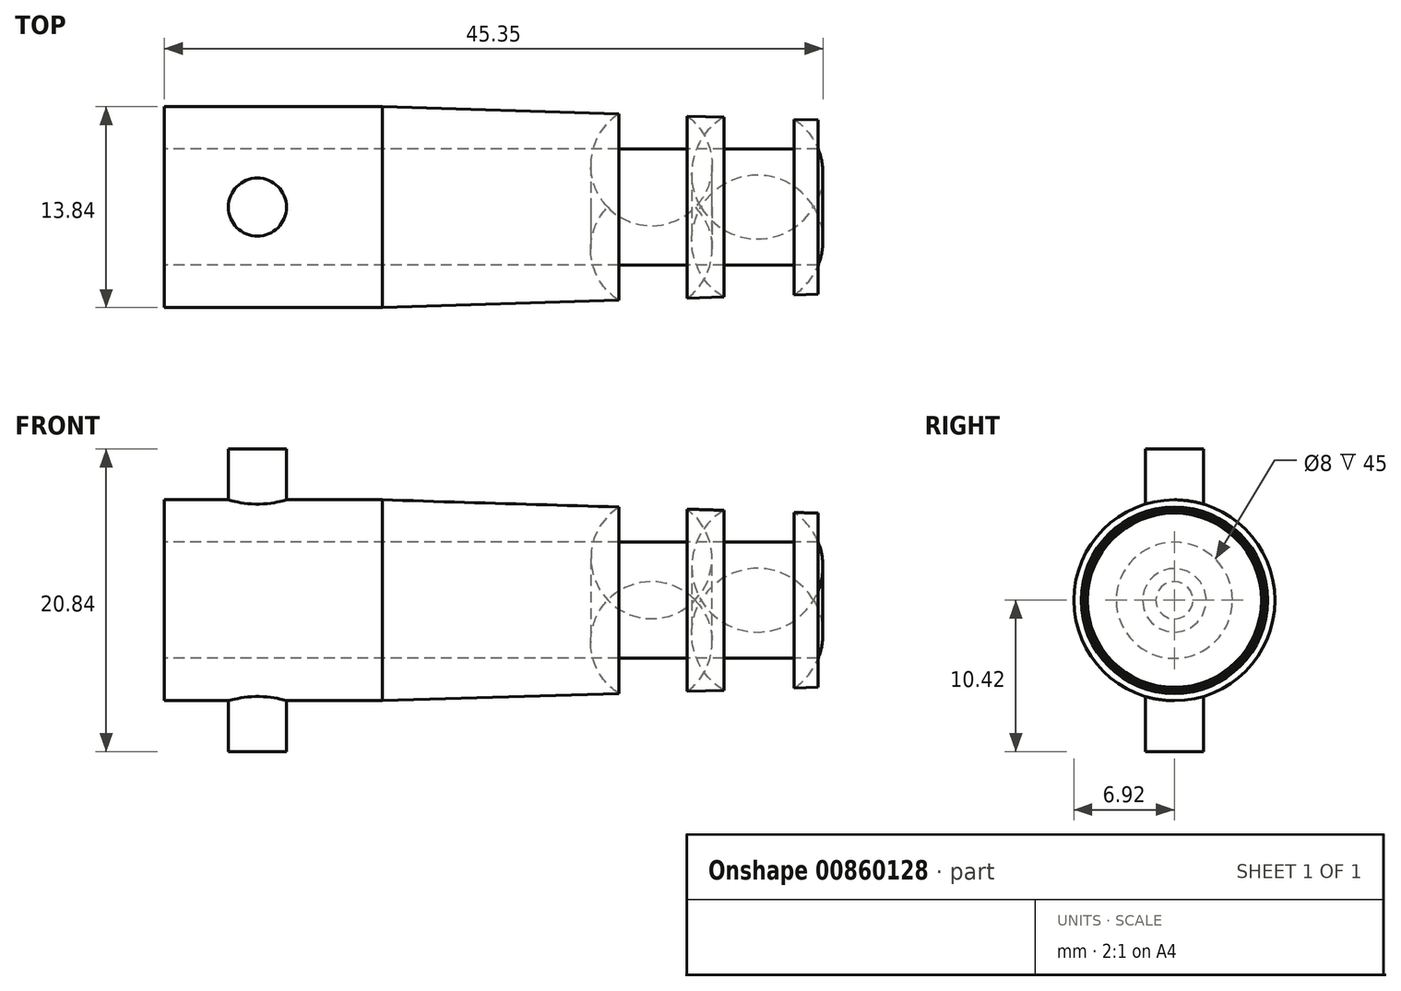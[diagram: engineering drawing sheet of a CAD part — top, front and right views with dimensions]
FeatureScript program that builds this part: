
annotation { "Feature Type Name" : "Feature", "Feature Type Description" : "" }
export const myFeature = defineFeature(function(context is Context, id is Id, definition is map)
    precondition{}
    {
        {
            var Q0;
            Q0=qCreatedBy(makeId("Front.planeOp"),FACE);
            var sketch = newSketch(context, id + "F0", { "sketchPlane" : qUnion([Q0])});
            skLineSegment(sketch, "E0", {"start": v(-34.69, 0) * mm, "end": v(10.31, 0) * mm});
            skLineSegment(sketch, "E1", {"start": v(10.31, 0) * mm, "end": v(10.31, 6) * mm});
            skLineSegment(sketch, "E2", {"start": v(-34.69, 6.92) * mm, "end": v(-19.69, 6.92) * mm});
            skLineSegment(sketch, "E3", {"start": v(-19.69, 6.92) * mm, "end": v(10.31, 6) * mm});
            skLineSegment(sketch, "E4", {"start": v(-34.69, 0) * mm, "end": v(-34.69, 6.92) * mm});
            skArc(sketch, "E5", {"start": v(8.68, 6.05) * mm, "mid": v(6.28, 6.83) * mm, "end": v(3.83, 6.2) * mm});
            skArc(sketch, "E6", {"start": v(1.31, 6.28) * mm, "mid": v(-1.02, 7.08) * mm, "end": v(-3.4, 6.42) * mm});
            skSolve(sketch);
        }
        {
            var Q0;
            {var subQ0=sQuery(id+"F0.wireOp",EDGE,"E6");Q0=makeQuery(id+"F0.imprint","IMPRINT",FACE,{"disambiguationData":[TD([[makeQuery(id+"F0.imprint","IMPRINT",EDGE,{"derivedFrom":subQ0}),1.0]])]});}
            var Q1;
            {var subQ0=sQuery(id+"F0.wireOp",EDGE,"E5");Q1=makeQuery(id+"F0.imprint","IMPRINT",FACE,{"disambiguationData":[TD([[makeQuery(id+"F0.imprint","IMPRINT",EDGE,{"derivedFrom":subQ0}),1.0]])]});}
            var Q2;
            Q2=makeQuery(id+"F0.imprint","IMPRINT",FACE,{"disambiguationData":[TD([[makeQuery(id+"F0.imprint","IMPRINT",EDGE,{"derivedFrom":sQuery(id+"F0.wireOp",EDGE,"E0")}),1.0]])]});
            var Q3;
            Q3=sQuery(id+"F0.wireOp",EDGE,"E0");
            revolve(context, id + "F1", {"surfaceOperationType" : NewSurfaceOperationType.NEW, "entities" : qUnion([Q0, Q1, Q2]), "axis" : qUnion([Q3]), "revolveType" : RevolveType.FULL});
        }
        {
            var Q0;
            Q0=qCreatedBy(makeId("Front.planeOp"),FACE);
            var sketch = newSketch(context, id + "F2", { "sketchPlane" : qUnion([Q0])});
            skPoint(sketch, "E7", {"position": v(-34.69, 6.92) * mm});
            skPoint(sketch, "E8", {"position": v(-34.69, -6.92) * mm});
            skLineSegment(sketch, "E9", {"start": v(-34.69, -6.92) * mm, "end": v(-30.29, -6.92) * mm, "construction": true});
            skLineSegment(sketch, "E10", {"start": v(-30.29, -6.92) * mm, "end": v(-30.29, -10.42) * mm});
            skLineSegment(sketch, "E11", {"start": v(-30.29, -10.42) * mm, "end": v(-28.29, -10.42) * mm});
            skLineSegment(sketch, "E12", {"start": v(-28.29, -10.42) * mm, "end": v(-28.29, -6.92) * mm});
            skLineSegment(sketch, "E13.MirrorCS", {"start": v(-28.29, 10.42) * mm, "end": v(-28.29, 6.92) * mm});
            skLineSegment(sketch, "E14.MirrorCS", {"start": v(-30.29, 6.92) * mm, "end": v(-30.29, 10.42) * mm});
            skLineSegment(sketch, "E15.MirrorCS", {"start": v(-30.29, 10.42) * mm, "end": v(-28.29, 10.42) * mm});
            skLineSegment(sketch, "E16", {"start": v(-30.29, -6.92) * mm, "end": v(-30.29, -6.02) * mm});
            skLineSegment(sketch, "E17", {"start": v(-30.29, -6.02) * mm, "end": v(-28.29, -6.02) * mm});
            skLineSegment(sketch, "E18", {"start": v(-28.29, -6.02) * mm, "end": v(-28.29, -6.92) * mm});
            skLineSegment(sketch, "E19", {"start": v(-30.29, 6.92) * mm, "end": v(-30.29, 5.47) * mm});
            skLineSegment(sketch, "E20", {"start": v(-30.29, 5.47) * mm, "end": v(-28.29, 5.47) * mm});
            skLineSegment(sketch, "E21", {"start": v(-28.29, 5.47) * mm, "end": v(-28.29, 6.92) * mm});
            skSolve(sketch);
        }
        {
            var Q0;
            Q0=makeQuery(id+"F2.imprint","IMPRINT",FACE,{"disambiguationData":[TD([[makeQuery(id+"F2.imprint","IMPRINT",EDGE,{"derivedFrom":sQuery(id+"F2.wireOp",EDGE,"RGX9hK7C-6vJY-tdlk-LFVB-kxxWvoX9Rff0")}),-1.0]])]});
            var Q1;
            Q1=makeQuery(id+"F2.imprint","IMPRINT",FACE,{"disambiguationData":[TD([[makeQuery(id+"F2.imprint","IMPRINT",EDGE,{"derivedFrom":sQuery(id+"F2.wireOp",EDGE,"E10")}),1.0]])]});
            var Q2;
            Q2=makeQuery(id+"F2.imprint","IMPRINT",FACE,{"disambiguationData":[TD([[makeQuery(id+"F2.imprint","IMPRINT",EDGE,{"derivedFrom":sQuery(id+"F2.wireOp",EDGE,"E13.MirrorCS")}),-1.0]])]});
            var Q3;
            Q3=sQuery(id+"F2.wireOp",EDGE,"E13.MirrorCS");
            revolve(context, id + "F3", {"operationType" : NewBodyOperationType.ADD, "surfaceOperationType" : NewSurfaceOperationType.NEW, "entities" : qUnion([Q0, Q1, Q2]), "axis" : qUnion([Q3]), "revolveType" : RevolveType.FULL});
        }
        {
            var Q0;
            Q0=makeQuery(id+"F1.opRevolve","SWEPT_FACE",FACE,{"disambiguationData":[OSD([sQuery(id+"F0.wireOp",EDGE,"E4")])]});
            var sketch = newSketch(context, id + "F4", { "sketchPlane" : qUnion([Q0])});
            skCircle(sketch, "E22", {"center": v(0, 0) * mm, "radius": 4 * mm});
            skSolve(sketch);
        }
        {
            var Q0;
            Q0 = qSketchRegion(id + "F4", true);
            extrude(context, id + "F5", {"entities" : qUnion([Q0]), "operationType" : NewBodyOperationType.REMOVE, "endBound" : BoundingType.UP_TO_NEXT, "oppositeDirection" : true, "depth" : 25 * mm, "offsetDistance" : 25 * mm});
        }
    });
